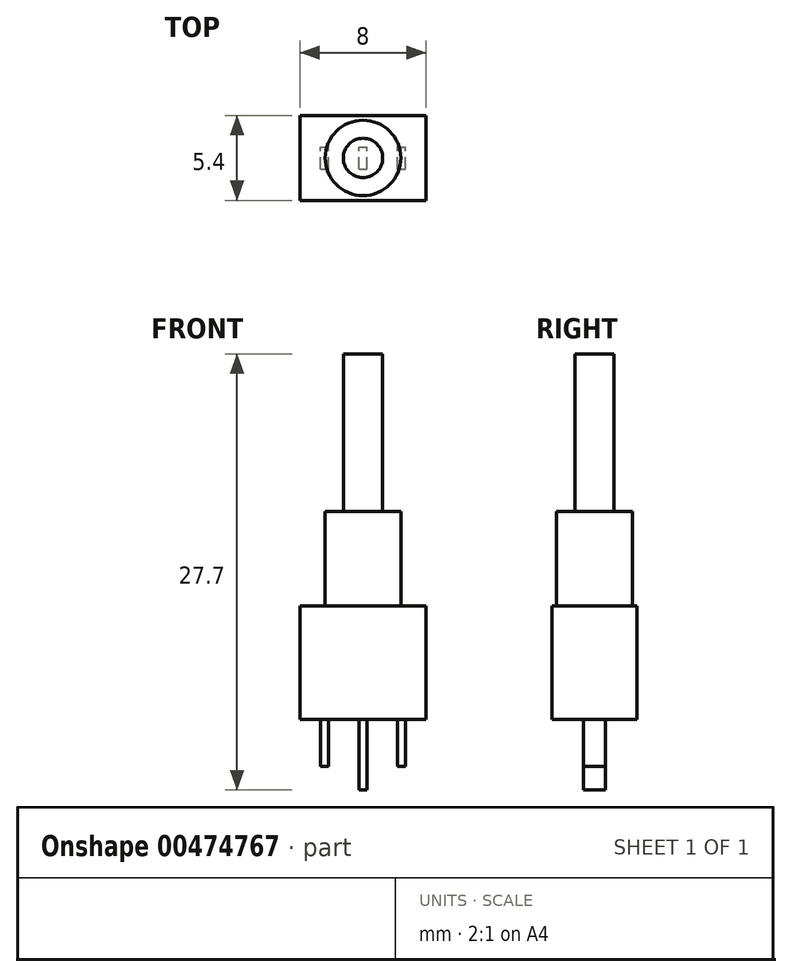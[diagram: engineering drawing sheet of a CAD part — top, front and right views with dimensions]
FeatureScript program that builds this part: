
annotation { "Feature Type Name" : "Feature", "Feature Type Description" : "" }
export const myFeature = defineFeature(function(context is Context, id is Id, definition is map)
    precondition{}
    {
        {
            var Q0;
            Q0=qCreatedBy(makeId("Front.planeOp"),FACE);
            var sketch = newSketch(context, id + "F0", { "sketchPlane" : qUnion([Q0])});
            skLineSegment(sketch, "E0.bottom", {"start": v(0, 0) * mm, "end": v(8, 0) * mm});
            skLineSegment(sketch, "E0.top", {"start": v(0, 7.2) * mm, "end": v(8, 7.2) * mm});
            skLineSegment(sketch, "E0.left", {"start": v(0, 0) * mm, "end": v(0, 7.2) * mm});
            skLineSegment(sketch, "E0.right", {"start": v(8, 0) * mm, "end": v(8, 7.2) * mm});
            skSolve(sketch);
        }
        {
            var Q0;
            Q0 = qSketchRegion(id + "F0", true);
            extrude(context, id + "F1", {"entities" : qUnion([Q0]), "depth" : 5.4 * mm});
        }
        {
            var Q0;
            Q0=makeQuery(id+"F1.opExtrude","SWEPT_FACE",FACE,{"disambiguationData":[OSD([sQuery(id+"F0.wireOp",EDGE,"E0.top")])]});
            var sketch = newSketch(context, id + "F2", { "sketchPlane" : qUnion([Q0])});
            skCircle(sketch, "E1", {"center": v(4, -2.7) * mm, "radius": 2.4 * mm});
            skSolve(sketch);
        }
        {
            var Q0;
            Q0 = qSketchRegion(id + "F2", true);
            extrude(context, id + "F3", {"entities" : qUnion([Q0]), "operationType" : NewBodyOperationType.ADD, "depth" : 6 * mm});
        }
        {
            var Q0;
            Q0=makeQuery(id+"F3.opExtrude","CAP_FACE",FACE,{"disambiguationData":[OSD([sQuery(id+"F2.wireOp",EDGE,"E1")])],"isStart":false});
            var sketch = newSketch(context, id + "F4", { "sketchPlane" : qUnion([Q0])});
            skCircle(sketch, "E2", {"center": v(4, -2.7) * mm, "radius": 1.25 * mm});
            skSolve(sketch);
        }
        {
            var Q0;
            Q0 = qSketchRegion(id + "F4", true);
            extrude(context, id + "F5", {"entities" : qUnion([Q0]), "operationType" : NewBodyOperationType.ADD, "depth" : 10 * mm});
        }
        {
            var Q0;
            Q0=makeQuery(id+"F1.opExtrude","SWEPT_FACE",FACE,{"disambiguationData":[OSD([sQuery(id+"F0.wireOp",EDGE,"E0.bottom")])]});
            var sketch = newSketch(context, id + "F6", { "sketchPlane" : qUnion([Q0])});
            skLineSegment(sketch, "E3.bottom", {"start": v(1.3, 3.4) * mm, "end": v(1.8, 3.4) * mm});
            skLineSegment(sketch, "E3.top", {"start": v(1.3, 2) * mm, "end": v(1.8, 2) * mm});
            skLineSegment(sketch, "E3.left", {"start": v(1.3, 3.4) * mm, "end": v(1.3, 2) * mm});
            skLineSegment(sketch, "E3.right", {"start": v(1.8, 3.4) * mm, "end": v(1.8, 2) * mm});
            skLineSegment(sketch, "E4.bottom", {"start": v(6.2, 3.4) * mm, "end": v(6.7, 3.4) * mm});
            skLineSegment(sketch, "E4.top", {"start": v(6.2, 2) * mm, "end": v(6.7, 2) * mm});
            skLineSegment(sketch, "E4.left", {"start": v(6.2, 3.4) * mm, "end": v(6.2, 2) * mm});
            skLineSegment(sketch, "E4.right", {"start": v(6.7, 3.4) * mm, "end": v(6.7, 2) * mm});
            skSolve(sketch);
        }
        {
            var Q0;
            Q0 = qSketchRegion(id + "F6", true);
            extrude(context, id + "F7", {"entities" : qUnion([Q0]), "operationType" : NewBodyOperationType.ADD, "depth" : 3 * mm});
        }
        {
            var Q0;
            Q0=makeQuery(id+"F1.opExtrude","SWEPT_FACE",FACE,{"disambiguationData":[OSD([sQuery(id+"F0.wireOp",EDGE,"E0.bottom")])]});
            var sketch = newSketch(context, id + "F8", { "sketchPlane" : qUnion([Q0])});
            skLineSegment(sketch, "E5.bottom", {"start": v(3.75, 3.4) * mm, "end": v(4.25, 3.4) * mm});
            skLineSegment(sketch, "E5.top", {"start": v(3.75, 2) * mm, "end": v(4.25, 2) * mm});
            skLineSegment(sketch, "E5.left", {"start": v(3.75, 3.4) * mm, "end": v(3.75, 2) * mm});
            skLineSegment(sketch, "E5.right", {"start": v(4.25, 3.4) * mm, "end": v(4.25, 2) * mm});
            skSolve(sketch);
        }
        {
            var Q0;
            Q0 = qSketchRegion(id + "F8", true);
            extrude(context, id + "F9", {"entities" : qUnion([Q0]), "operationType" : NewBodyOperationType.ADD, "depth" : 4.5 * mm});
        }
    });
